# Revit family: BAS-IP_Вызывная панель_AV-03BD
name_source: partatom
category: Устройства связи
units: mm (PartAtom-declared; Revit-internal decimal feet)

## family parameters
Всегда вертикально = Да
На основе рабочей плоскости = Нет
Общий = Нет
При загрузке вырезать с полостями = Нет
Размер круглого соединителя = Использовать диаметр
Сохранять ориентацию аннотаций = Нет
Тип детали = Нормальный
Точка расчета площади = Нет

## types (2) — shared parameters
ADSK_Единица измерения = шт.
ADSK_Завод-изготовитель = BAS-IP
ADSK_Количество = 1
ADSK_Наименование = Индивидуальная IP вызывная панель в пластиковом корпусе, с сенсорной кнопкой и UKEY
IK-код = IK06
Выходное видео = HD (1280 × 720), H.264 Main Profile
Дисплей = Нет
Изготовитель = BAS-IP
Камера = 1/4”
Класс степени защиты = IP64
Корпус = АБС-пластик
Минимальная освещенность = 0,01 Люкс
Ночная подсветка = 6 светодиодов
Питание = PoE 802.3af, +12 В постоянного тока
Потребление питания = 6,5 Вт, в режиме ожидания - 2,5 Вт
Размер под установку = 111,3 × 170,4 × 73 мм
Размер самой панели = 102 × 160 × 46 мм
Разрешение = 2 Мп
Температурный режим = -40 – +65 °С
Тип панели = Индивидуальная
Тип установки = Накладной монтаж с накладкой и без (кронштейны в комплекте)
Угол обзора камеры = 90° (по горизонтали)

## per-type parameters (varying)
| type | ADSK_Марка | ADSK_Материал |
| Серебристый | AV-03BD Silver | Silver |
| Черный | AV-03BD Black | Black silver |

note: column(s) folded — value = type name in every type: Цветовое решение
